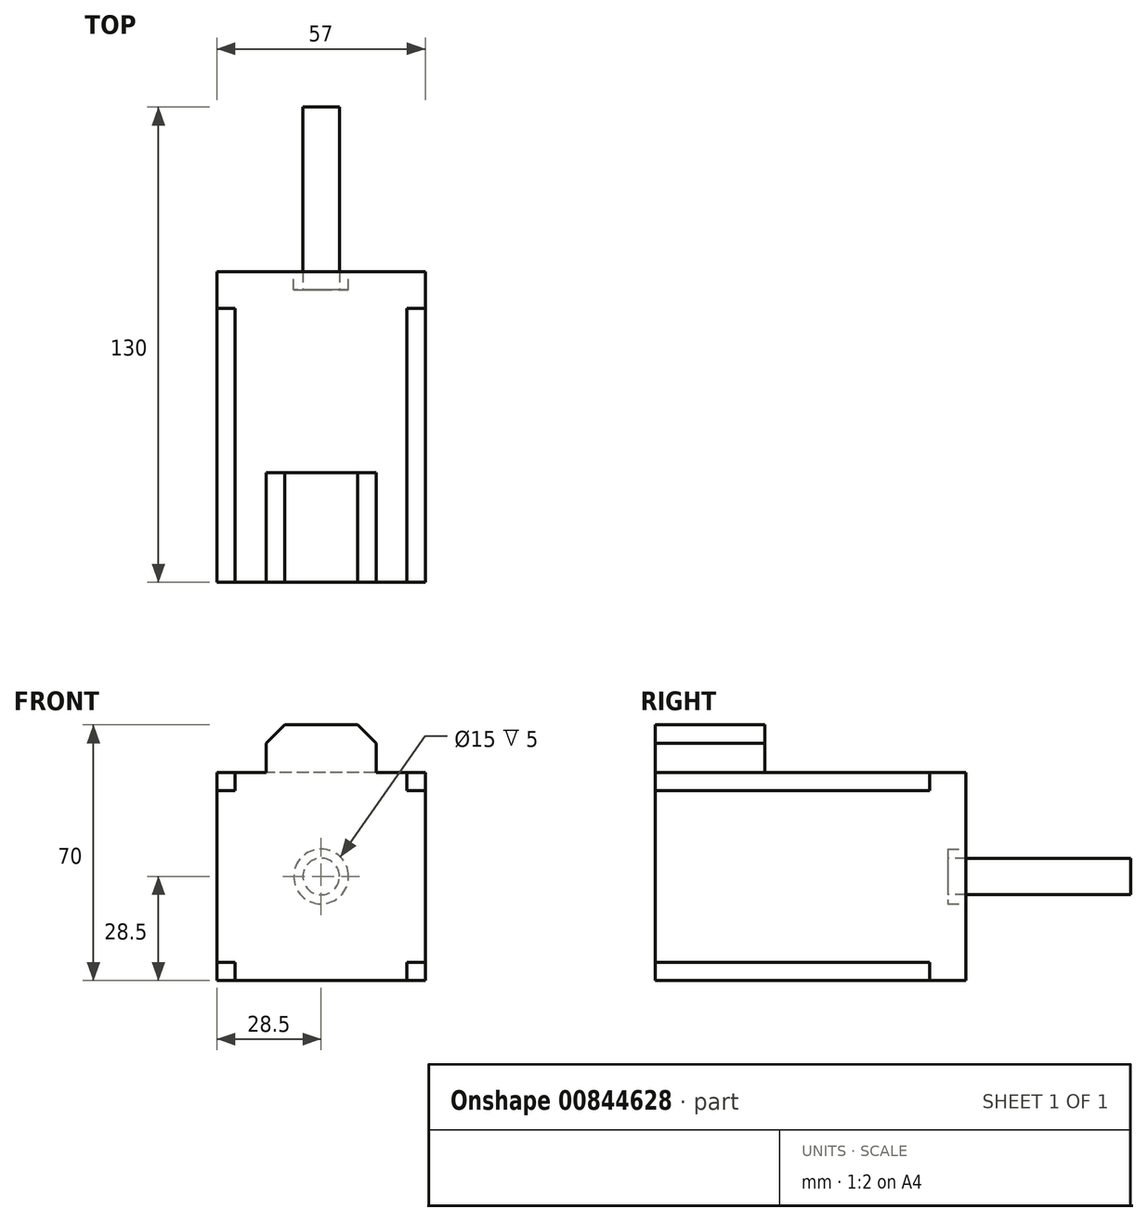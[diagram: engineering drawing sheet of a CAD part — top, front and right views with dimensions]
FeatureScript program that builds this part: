
annotation { "Feature Type Name" : "Feature", "Feature Type Description" : "" }
export const myFeature = defineFeature(function(context is Context, id is Id, definition is map)
    precondition{}
    {
        {
            var Q0;
            Q0=qCreatedBy(makeId("Front.planeOp"),FACE);
            var sketch = newSketch(context, id + "F0", { "sketchPlane" : qUnion([Q0])});
            skLineSegment(sketch, "E0.bottom", {"start": v(28.5, -28.5) * mm, "end": v(-28.5, -28.5) * mm});
            skLineSegment(sketch, "E0.top", {"start": v(28.5, 28.5) * mm, "end": v(-28.5, 28.5) * mm});
            skLineSegment(sketch, "E0.left", {"start": v(28.5, -28.5) * mm, "end": v(28.5, 28.5) * mm});
            skLineSegment(sketch, "E0.right", {"start": v(-28.5, -28.5) * mm, "end": v(-28.5, 28.5) * mm});
            skPoint(sketch, "E0.middle", {"position": v(0, 0) * mm});
            skSolve(sketch);
        }
        {
            var Q0;
            Q0=makeQuery(id+"F0.imprint","IMPRINT",FACE,{"disambiguationData":[TD([[makeQuery(id+"F0.imprint","IMPRINT",EDGE,{"derivedFrom":sQuery(id+"F0.wireOp",EDGE,"E0.bottom")}),-1.0]])]});
            extrude(context, id + "F1", {"entities" : qUnion([Q0]), "depth" : 10 * mm, "offsetDistance" : 25 * mm});
        }
        {
            var Q0;
            Q0=makeQuery(id+"F1.opExtrude","CAP_FACE",FACE,{"disambiguationData":[OSD([sQuery(id+"F0.wireOp",EDGE,"E0.bottom"),sQuery(id+"F0.wireOp",EDGE,"E0.top"),sQuery(id+"F0.wireOp",EDGE,"E0.left"),sQuery(id+"F0.wireOp",EDGE,"E0.right")])],"isStart":true});
            var sketch = newSketch(context, id + "F2", { "sketchPlane" : qUnion([Q0])});
            skLineSegment(sketch, "E1.0", {"start": v(-23.5, -28.5) * mm, "end": v(-23.5, 28.5) * mm});
            skLineSegment(sketch, "E2.0", {"start": v(-28.5, 23.5) * mm, "end": v(28.5, 23.5) * mm});
            skLineSegment(sketch, "E3.0", {"start": v(23.5, -28.5) * mm, "end": v(23.5, 28.5) * mm});
            skLineSegment(sketch, "E4.0", {"start": v(-28.5, -23.5) * mm, "end": v(28.5, -23.5) * mm});
            skSolve(sketch);
        }
        {
            var Q0;
            {var subQ0=sQuery(id+"F2.wireOp",EDGE,"E4.0");var subQ1=sQuery(id+"F2.wireOp",EDGE,"E1.0");var subQ2=makeQuery(id+"F2.imprint","INTERSECT",VERTEX,{"derivedFrom":[subQ1,subQ0]});Q0=makeQuery(id+"F2.imprint","IMPRINT",FACE,{"disambiguationData":[TD([[makeQuery(id+"F2.imprint","IMPRINT",EDGE,{"disambiguationData":[TD([[subQ2,-1.0]])],"derivedFrom":subQ1}),1.0]])]});}
            var Q1;
            {var subQ0=sQuery(id+"F2.wireOp",EDGE,"E1.0");var subQ1=makeQuery(id+"F1.opExtrude","CAP_EDGE",EDGE,{"disambiguationData":[OSD([sQuery(id+"F0.wireOp",EDGE,"E0.top")])],"isStart":true});var subQ2=makeQuery(id+"F2.imprint","INTERSECT",VERTEX,{"derivedFrom":[subQ1,subQ0]});Q1=makeQuery(id+"F2.imprint","IMPRINT",FACE,{"disambiguationData":[TD([[makeQuery(id+"F2.imprint","IMPRINT",EDGE,{"disambiguationData":[TD([[subQ2,1.0]])],"derivedFrom":subQ0}),-1.0]])]});}
            var Q2;
            {var subQ0=sQuery(id+"F2.wireOp",EDGE,"E2.0");var subQ1=makeQuery(id+"F1.opExtrude","CAP_EDGE",EDGE,{"disambiguationData":[OSD([sQuery(id+"F0.wireOp",EDGE,"E0.right")])],"isStart":true});var subQ2=makeQuery(id+"F2.imprint","INTERSECT",VERTEX,{"derivedFrom":[subQ1,subQ0]});Q2=makeQuery(id+"F2.imprint","IMPRINT",FACE,{"disambiguationData":[TD([[makeQuery(id+"F2.imprint","IMPRINT",EDGE,{"disambiguationData":[TD([[subQ2,1.0]])],"derivedFrom":subQ0}),-1.0]])]});}
            var Q3;
            {var subQ0=sQuery(id+"F2.wireOp",EDGE,"E4.0");var subQ1=sQuery(id+"F2.wireOp",EDGE,"E1.0");var subQ2=makeQuery(id+"F2.imprint","INTERSECT",VERTEX,{"derivedFrom":[subQ1,subQ0]});Q3=makeQuery(id+"F2.imprint","IMPRINT",FACE,{"disambiguationData":[TD([[makeQuery(id+"F2.imprint","IMPRINT",EDGE,{"disambiguationData":[TD([[subQ2,-1.0]])],"derivedFrom":subQ1}),-1.0]])]});}
            var Q4;
            {var subQ0=sQuery(id+"F2.wireOp",EDGE,"E1.0");var subQ1=makeQuery(id+"F1.opExtrude","CAP_EDGE",EDGE,{"disambiguationData":[OSD([sQuery(id+"F0.wireOp",EDGE,"E0.bottom")])],"isStart":true});var subQ2=makeQuery(id+"F2.imprint","INTERSECT",VERTEX,{"derivedFrom":[subQ1,subQ0]});Q4=makeQuery(id+"F2.imprint","IMPRINT",FACE,{"disambiguationData":[TD([[makeQuery(id+"F2.imprint","IMPRINT",EDGE,{"disambiguationData":[TD([[subQ2,-1.0]])],"derivedFrom":subQ0}),-1.0]])]});}
            extrude(context, id + "F3", {"entities" : qUnion([Q0, Q1, Q2, Q3, Q4]), "operationType" : NewBodyOperationType.ADD, "oppositeDirection" : true, "depth" : 85 * mm, "offsetDistance" : 25 * mm});
        }
        {
            var Q0;
            Q0=makeQuery(id+"F3.opExtrude","CAP_FACE",FACE,{"disambiguationData":[OSD([sQuery(id+"F0.wireOp",EDGE,"E0.bottom"),sQuery(id+"F0.wireOp",EDGE,"E0.top"),sQuery(id+"F0.wireOp",EDGE,"E0.left"),sQuery(id+"F0.wireOp",EDGE,"E0.right"),sQuery(id+"F2.wireOp",EDGE,"E1.0"),sQuery(id+"F2.wireOp",EDGE,"E2.0"),sQuery(id+"F2.wireOp",EDGE,"E3.0"),sQuery(id+"F2.wireOp",EDGE,"E4.0")])],"isStart":false});
            var sketch = newSketch(context, id + "F4", { "sketchPlane" : qUnion([Q0])});
            skLineSegment(sketch, "E5.top", {"start": v(15, 41.5) * mm, "end": v(-15, 41.5) * mm});
            skLineSegment(sketch, "E5.left", {"start": v(15, 28.5) * mm, "end": v(15, 41.5) * mm});
            skLineSegment(sketch, "E5.right", {"start": v(-15, 28.5) * mm, "end": v(-15, 41.5) * mm});
            skLineSegment(sketch, "E6", {"start": v(-15, 28.5) * mm, "end": v(15, 28.5) * mm});
            skSolve(sketch);
        }
        {
            var Q0;
            Q0=makeQuery(id+"F4.imprint","IMPRINT",FACE,{"disambiguationData":[TD([[makeQuery(id+"F4.imprint","IMPRINT",EDGE,{"derivedFrom":sQuery(id+"F4.wireOp",EDGE,"E5.top")}),1.0]])]});
            extrude(context, id + "F5", {"entities" : qUnion([Q0]), "operationType" : NewBodyOperationType.ADD, "oppositeDirection" : true, "depth" : 30 * mm, "offsetDistance" : 25 * mm});
        }
        {
            var Q0;
            Q0=makeQuery(id+"F5.opExtrude","SWEPT_EDGE",EDGE,{"disambiguationData":[OSD([sQuery(id+"F4.wireOp",EDGE,"E5.top"),sQuery(id+"F4.wireOp",EDGE,"E5.left")])]});
            var Q1;
            Q1=makeQuery(id+"F5.opExtrude","SWEPT_EDGE",EDGE,{"disambiguationData":[OSD([sQuery(id+"F4.wireOp",EDGE,"E5.top"),sQuery(id+"F4.wireOp",EDGE,"E5.right")])]});
            chamfer(context, id + "F6", {"entities" : qUnion([Q0, Q1]), "width" : 5 * mm, "tangentPropagation" : true});
        }
        {
            var Q0;
            Q0=makeQuery(id+"F1.opExtrude","CAP_FACE",FACE,{"disambiguationData":[OSD([sQuery(id+"F0.wireOp",EDGE,"E0.bottom"),sQuery(id+"F0.wireOp",EDGE,"E0.top"),sQuery(id+"F0.wireOp",EDGE,"E0.left"),sQuery(id+"F0.wireOp",EDGE,"E0.right")])],"isStart":true});
            var sketch = newSketch(context, id + "F7", { "sketchPlane" : qUnion([Q0])});
            skCircle(sketch, "E7", {"center": v(0, 0) * mm, "radius": 7.5 * mm});
            skSolve(sketch);
        }
        {
            var Q0;
            Q0 = qSketchRegion(id + "F7", true);
            extrude(context, id + "F8", {"entities" : qUnion([Q0]), "operationType" : NewBodyOperationType.REMOVE, "oppositeDirection" : true, "depth" : 5 * mm, "offsetDistance" : 25 * mm});
        }
        {
            var Q0;
            Q0=makeQuery(id+"F8.boolean.opBoolean","COPY",FACE,{"derivedFrom":makeQuery(id+"F8.opExtrude","CAP_FACE",FACE,{"disambiguationData":[OSD([sQuery(id+"F7.wireOp",EDGE,"E7")])],"isStart":false})});
            var sketch = newSketch(context, id + "F9", { "sketchPlane" : qUnion([Q0])});
            skCircle(sketch, "E8", {"center": v(0, 0) * mm, "radius": 5 * mm});
            skSolve(sketch);
        }
        {
            var Q0;
            Q0=makeQuery(id+"F9.imprint","IMPRINT",FACE,{"disambiguationData":[TD([[makeQuery(id+"F9.imprint","IMPRINT",EDGE,{"derivedFrom":sQuery(id+"F9.wireOp",EDGE,"E8")}),1.0]])]});
            extrude(context, id + "F10", {"entities" : qUnion([Q0]), "operationType" : NewBodyOperationType.ADD, "depth" : 50 * mm, "offsetDistance" : 25 * mm});
        }
    });
